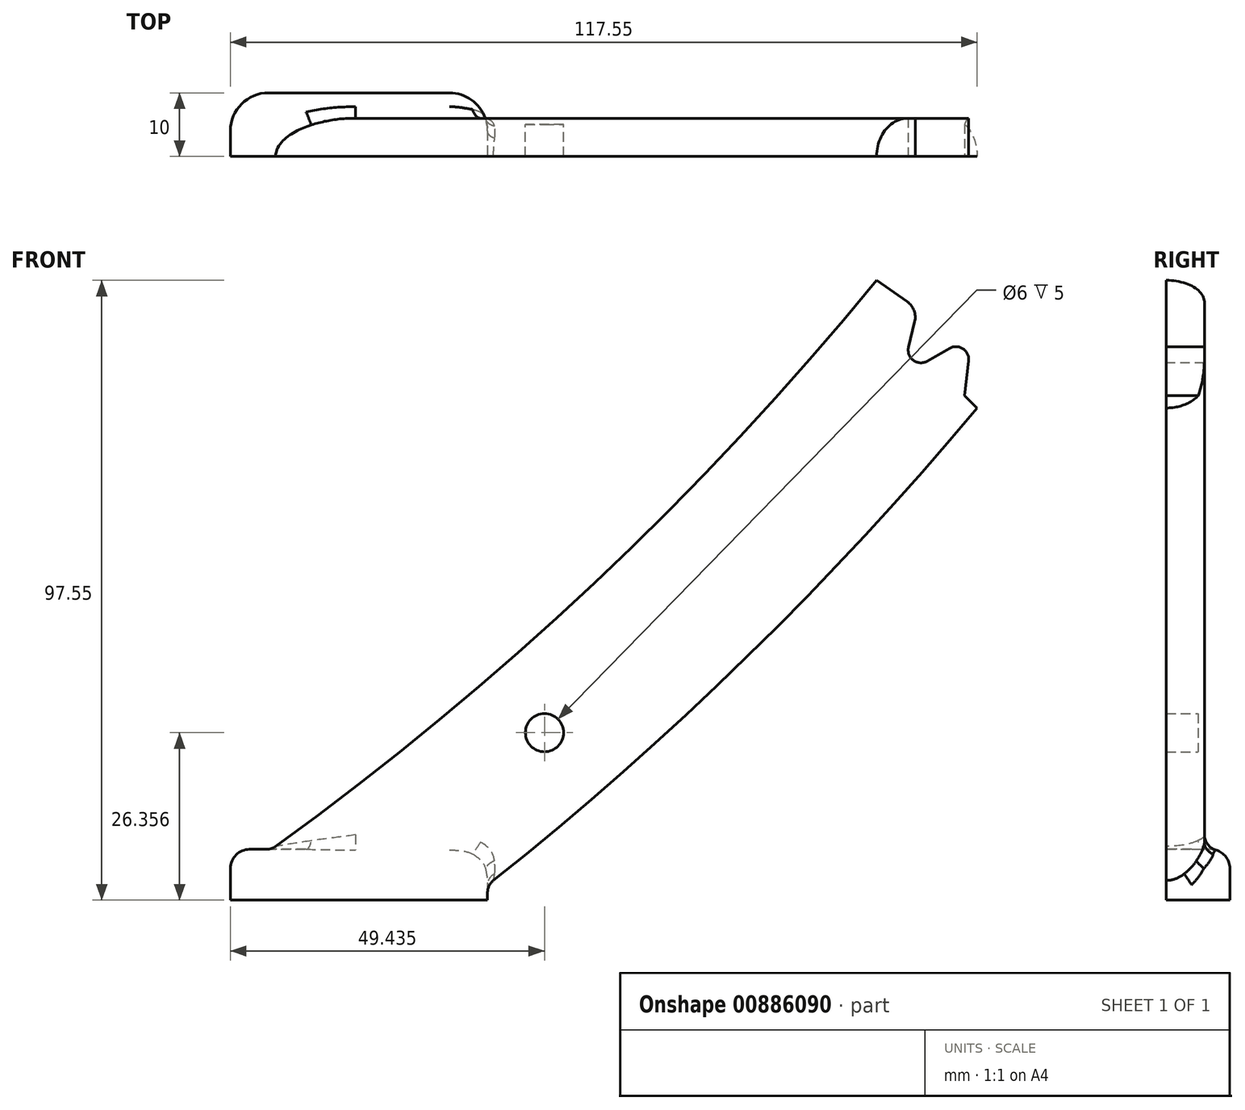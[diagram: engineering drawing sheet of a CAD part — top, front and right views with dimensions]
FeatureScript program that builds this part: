
annotation { "Feature Type Name" : "Feature", "Feature Type Description" : "" }
export const myFeature = defineFeature(function(context is Context, id is Id, definition is map)
    precondition{}
    {
        {
            var Q0;
            Q0=qCreatedBy(makeId("Front.planeOp"),FACE);
            var sketch = newSketch(context, id + "F0", { "sketchPlane" : qUnion([Q0])});
            skLineSegment(sketch, "E0", {"start": v(0, 0) * mm, "end": v(-44.34, 296.7) * mm, "construction": true});
            skLineSegment(sketch, "E1", {"start": v(0, 0) * mm, "end": v(-300, 0) * mm, "construction": true});
            skCircle(sketch, "E2", {"center": v(0, 0) * mm, "radius": 200 * mm, "construction": true});
            skArc(sketch, "E3", {"start": v(-200, 0) * mm, "mid": v(-101.64, 87.58) * mm, "end": v(-29.56, 197.8) * mm});
            skArc(sketch, "E4", {"start": v(-157.53, 0) * mm, "mid": v(-82.7, 71.26) * mm, "end": v(-23.28, 155.8) * mm});
            skLineSegment(sketch, "E5", {"start": v(-23.28, 155.8) * mm, "end": v(-29.56, 197.8) * mm});
            skLineSegment(sketch, "E6", {"start": v(-157.53, 0) * mm, "end": v(-200, 0) * mm});
            skSolve(sketch);
        }
        {
            var Q0;
            Q0 = qSketchRegion(id + "F0", true);
            extrude(context, id + "F1", {"entities" : qUnion([Q0]), "depth" : 12 * mm, "offsetDistance" : 25 * mm});
        }
        {
            var Q0;
            Q0=makeQuery(id+"F1.opExtrude","CAP_EDGE",EDGE,{"disambiguationData":[OSD([sQuery(id+"F0.wireOp",EDGE,"E3")])],"isStart":false});
            var Q1;
            Q1=makeQuery(id+"F1.opExtrude","CAP_EDGE",EDGE,{"disambiguationData":[OSD([sQuery(id+"F0.wireOp",EDGE,"E3")])],"isStart":true});
            var Q2;
            Q2=makeQuery(id+"F1.opExtrude","CAP_EDGE",EDGE,{"disambiguationData":[OSD([sQuery(id+"F0.wireOp",EDGE,"E4")])],"isStart":true});
            var Q3;
            Q3=makeQuery(id+"F1.opExtrude","CAP_EDGE",EDGE,{"disambiguationData":[OSD([sQuery(id+"F0.wireOp",EDGE,"E4")])],"isStart":false});
            fillet(context, id + "F2", {"entities" : qUnion([Q0, Q1, Q2, Q3]), "radius" : 6 * mm, "tangentPropagation" : true, "allowEdgeOverflow" : false});
        }
        {
            var Q0;
            Q0=makeQuery(id+"F1.opExtrude","SWEPT_FACE",FACE,{"disambiguationData":[OSD([sQuery(id+"F0.wireOp",EDGE,"E5")])]});
            var sketch = newSketch(context, id + "F3", { "sketchPlane" : qUnion([Q0])});
            skLineSegment(sketch, "E7.bottom", {"start": v(23, 157.53) * mm, "end": v(-35, 157.53) * mm, "construction": true});
            skLineSegment(sketch, "E7.top", {"start": v(23, 200) * mm, "end": v(-35, 200) * mm, "construction": true});
            skLineSegment(sketch, "E7.left", {"start": v(23, 157.53) * mm, "end": v(23, 200) * mm, "construction": true});
            skLineSegment(sketch, "E7.right", {"start": v(-35, 157.53) * mm, "end": v(-35, 200) * mm, "construction": true});
            skPoint(sketch, "E7.middle", {"position": v(-6, 178.76) * mm});
            skLineSegment(sketch, "E8", {"start": v(-12.34, 197.4) * mm, "end": v(-32.11, 188.18) * mm});
            skLineSegment(sketch, "E9", {"start": v(-32.11, 169.31) * mm, "end": v(-6.84, 157.53) * mm});
            skLineSegment(sketch, "E10", {"start": v(-5.16, 157.53) * mm, "end": v(20.11, 169.31) * mm});
            skLineSegment(sketch, "E11", {"start": v(-35, 183.65) * mm, "end": v(-35, 173.84) * mm});
            skLineSegment(sketch, "E12", {"start": v(23, 173.84) * mm, "end": v(23, 183.65) * mm});
            skPoint(sketch, "E13.visualSharp", {"position": v(23, 185.54) * mm});
            skArc(sketch, "E13.filletArc", {"start": v(23, 183.65) * mm, "mid": v(22.22, 186.34) * mm, "end": v(20.11, 188.18) * mm});
            skPoint(sketch, "E14.visualSharp", {"position": v(23, 170.66) * mm});
            skArc(sketch, "E14.filletArc", {"start": v(20.11, 169.31) * mm, "mid": v(22.22, 171.16) * mm, "end": v(23, 173.84) * mm});
            skPoint(sketch, "E15.visualSharp", {"position": v(-35, 170.66) * mm});
            skArc(sketch, "E15.filletArc", {"start": v(-35, 173.84) * mm, "mid": v(-34.22, 171.16) * mm, "end": v(-32.11, 169.31) * mm});
            skPoint(sketch, "E16.visualSharp", {"position": v(-35, 186.84) * mm});
            skArc(sketch, "E16.filletArc", {"start": v(-32.11, 188.18) * mm, "mid": v(-34.22, 186.34) * mm, "end": v(-35, 183.65) * mm});
            skLineSegment(sketch, "E17", {"start": v(-6.84, 157.53) * mm, "end": v(-5.16, 157.53) * mm});
            skArc(sketch, "E18", {"start": v(0.34, 197.4) * mm, "mid": v(-6, 198.8) * mm, "end": v(-12.34, 197.4) * mm});
            skLineSegment(sketch, "E19.trimOffspring", {"start": v(0.34, 197.4) * mm, "end": v(20.11, 188.18) * mm});
            skSolve(sketch);
        }
        {
            var Q0;
            Q0 = qSketchRegion(id + "F3", true);
            extrude(context, id + "F4", {"entities" : qUnion([Q0]), "operationType" : NewBodyOperationType.ADD, "oppositeDirection" : true, "depth" : 8 * mm, "offsetDistance" : 25 * mm});
        }
        {
            var Q0;
            Q0=makeQuery(id+"F4.boolean.opBoolean","INTERSECT",EDGE,{"derivedFrom":[makeQuery(id+"F2.opFillet","BLEND_FACE",FACE,{"disambiguationData":[OSD([sQuery(id+"F0.wireOp",EDGE,"E3")])]}),makeQuery(id+"F4.opExtrude","CAP_FACE",FACE,{"disambiguationData":[OSD([sQuery(id+"F3.wireOp",EDGE,"RdZrtCav-a8Ya-EYjV-l5Lc-FXPEVfNipvTb"),sQuery(id+"F3.wireOp",EDGE,"E8"),sQuery(id+"F3.wireOp",EDGE,"E9"),sQuery(id+"F3.wireOp",EDGE,"E10"),sQuery(id+"F3.wireOp",EDGE,"E11"),sQuery(id+"F3.wireOp",EDGE,"E12"),sQuery(id+"F3.wireOp",EDGE,"E13.filletArc"),sQuery(id+"F3.wireOp",EDGE,"E14.filletArc"),sQuery(id+"F3.wireOp",EDGE,"E15.filletArc"),sQuery(id+"F3.wireOp",EDGE,"E16.filletArc"),sQuery(id+"F3.wireOp",EDGE,"WmkRQfoL-1Tcq-6rLF-DuZA-oRjccm2ZQQoJ"),sQuery(id+"F3.wireOp",EDGE,"E17")])],"isStart":false})]});
            fillet(context, id + "F5", {"entities" : qUnion([Q0]), "radius" : 5 * mm, "tangentPropagation" : true, "allowEdgeOverflow" : false});
        }
        {
            var Q0;
            Q0=makeQuery(id+"F4.opExtrude","CAP_EDGE",EDGE,{"disambiguationData":[OSD([sQuery(id+"F3.wireOp",EDGE,"E19.trimOffspring")])],"isStart":false});
            fillet(context, id + "F6", {"entities" : qUnion([Q0]), "radius" : 5 * mm, "tangentPropagation" : true, "allowEdgeOverflow" : false});
        }
        {
            var Q0;
            Q0=makeQuery(id+"F1.opExtrude","SWEPT_FACE",FACE,{"disambiguationData":[OSD([sQuery(id+"F0.wireOp",EDGE,"E6")])]});
            var sketch = newSketch(context, id + "F7", { "sketchPlane" : qUnion([Q0])});
            skLineSegment(sketch, "E20.bottom", {"start": v(-160.53, -4) * mm, "end": v(-189, -4) * mm});
            skLineSegment(sketch, "E20.top", {"start": v(-160.53, 16) * mm, "end": v(-189, 16) * mm});
            skLineSegment(sketch, "E20.left", {"start": v(-154.53, 2) * mm, "end": v(-154.53, 10) * mm});
            skLineSegment(sketch, "E20.right", {"start": v(-195, 2) * mm, "end": v(-195, 10) * mm});
            skPoint(sketch, "E20.middle", {"position": v(-174.76, 6) * mm});
            skPoint(sketch, "E21.visualSharp", {"position": v(-195, 16) * mm});
            skArc(sketch, "E21.filletArc", {"start": v(-189, 16) * mm, "mid": v(-193.24, 14.24) * mm, "end": v(-195, 10) * mm});
            skPoint(sketch, "E22.visualSharp", {"position": v(-154.53, 16) * mm});
            skArc(sketch, "E22.filletArc", {"start": v(-154.53, 10) * mm, "mid": v(-156.28, 14.24) * mm, "end": v(-160.53, 16) * mm});
            skPoint(sketch, "E23.visualSharp", {"position": v(-154.53, -4) * mm});
            skArc(sketch, "E23.filletArc", {"start": v(-160.53, -4) * mm, "mid": v(-156.28, -2.24) * mm, "end": v(-154.53, 2) * mm});
            skPoint(sketch, "E24.visualSharp", {"position": v(-195, -4) * mm});
            skArc(sketch, "E24.filletArc", {"start": v(-195, 2) * mm, "mid": v(-193.24, -2.24) * mm, "end": v(-189, -4) * mm});
            skSolve(sketch);
        }
        {
            var Q0;
            Q0 = qSketchRegion(id + "F7", true);
            extrude(context, id + "F8", {"entities" : qUnion([Q0]), "operationType" : NewBodyOperationType.ADD, "oppositeDirection" : true, "depth" : 8 * mm, "offsetDistance" : 25 * mm});
        }
        {
            var Q0;
            Q0=makeQuery(id+"F8.opExtrude","CAP_EDGE",EDGE,{"disambiguationData":[OSD([sQuery(id+"F7.wireOp",EDGE,"E20.bottom")])],"isStart":false});
            fillet(context, id + "F9", {"entities" : qUnion([Q0]), "radius" : 3 * mm, "tangentPropagation" : true, "allowEdgeOverflow" : false});
        }
        {
            var Q0;
            Q0=makeQuery(id+"F8.boolean.opBoolean","INTERSECT",EDGE,{"derivedFrom":[makeQuery(id+"F1.opExtrude","CAP_FACE",FACE,{"disambiguationData":[OSD([sQuery(id+"F0.wireOp",EDGE,"E3"),sQuery(id+"F0.wireOp",EDGE,"E4"),sQuery(id+"F0.wireOp",EDGE,"E5"),sQuery(id+"F0.wireOp",EDGE,"E6")])],"isStart":true}),makeQuery(id+"F8.opExtrude","CAP_FACE",FACE,{"disambiguationData":[OSD([sQuery(id+"F7.wireOp",EDGE,"E20.bottom"),sQuery(id+"F7.wireOp",EDGE,"E20.top"),sQuery(id+"F7.wireOp",EDGE,"E20.left"),sQuery(id+"F7.wireOp",EDGE,"E20.right"),sQuery(id+"F7.wireOp",EDGE,"E21.filletArc"),sQuery(id+"F7.wireOp",EDGE,"E22.filletArc"),sQuery(id+"F7.wireOp",EDGE,"E23.filletArc"),sQuery(id+"F7.wireOp",EDGE,"E24.filletArc")])],"isStart":false})]});
            fillet(context, id + "F10", {"entities" : qUnion([Q0]), "radius" : 2.5 * mm, "tangentPropagation" : true, "allowEdgeOverflow" : false});
        }
        {
            var Q0;
            Q0=makeQuery(id+"F8.boolean.opBoolean","MERGE",FACE,{"derivedFrom":[makeQuery(id+"F1.opExtrude","SWEPT_FACE",FACE,{"disambiguationData":[OSD([sQuery(id+"F0.wireOp",EDGE,"E6")])]}),makeQuery(id+"F8.opExtrude","CAP_FACE",FACE,{"disambiguationData":[OSD([sQuery(id+"F7.wireOp",EDGE,"E20.bottom"),sQuery(id+"F7.wireOp",EDGE,"E20.top"),sQuery(id+"F7.wireOp",EDGE,"E20.left"),sQuery(id+"F7.wireOp",EDGE,"E20.right"),sQuery(id+"F7.wireOp",EDGE,"E21.filletArc"),sQuery(id+"F7.wireOp",EDGE,"E22.filletArc"),sQuery(id+"F7.wireOp",EDGE,"E23.filletArc"),sQuery(id+"F7.wireOp",EDGE,"E24.filletArc")])],"isStart":true})]});
            var sketch = newSketch(context, id + "F11", { "sketchPlane" : qUnion([Q0])});
            skArc(sketch, "E25", {"start": v(-194.9, 0.87) * mm, "mid": v(-192.82, -2.62) * mm, "end": v(-189, -4) * mm});
            skArc(sketch, "E26", {"start": v(-189, 16) * mm, "mid": v(-192.82, 14.62) * mm, "end": v(-194.9, 11.13) * mm});
            skLineSegment(sketch, "E27", {"start": v(-189, -4) * mm, "end": v(-189.9, -7.83) * mm});
            skLineSegment(sketch, "E28", {"start": v(-189.9, -7.83) * mm, "end": v(-199.49, -1.04) * mm});
            skLineSegment(sketch, "E29", {"start": v(-199.49, -1.04) * mm, "end": v(-201.87, 5.8) * mm});
            skLineSegment(sketch, "E30", {"start": v(-201.87, 5.8) * mm, "end": v(-200.5, 12.71) * mm});
            skLineSegment(sketch, "E31", {"start": v(-200.5, 12.71) * mm, "end": v(-193.47, 21.42) * mm});
            skLineSegment(sketch, "E32", {"start": v(-193.47, 21.42) * mm, "end": v(-189, 16) * mm});
            skLineSegment(sketch, "E33.0.1", {"start": v(-195, 10) * mm, "end": v(-195, 2) * mm});
            skFitSpline(sketch, "E33.0.3", {"points": [v(-195, 2) * mm, v(-195, 4.67) * mm, v(-195, 7.33) * mm, v(-195, 10) * mm]});
            skArc(sketch, "E34", {"start": v(-195, 2) * mm, "mid": v(-194.97, 1.43) * mm, "end": v(-194.9, 0.87) * mm});
            skArc(sketch, "E35", {"start": v(-194.9, 11.13) * mm, "mid": v(-194.97, 10.57) * mm, "end": v(-195, 10) * mm});
            skSolve(sketch);
        }
        {
            var Q0;
            Q0 = qSketchRegion(id + "F11", true);
            extrude(context, id + "F12", {"entities" : qUnion([Q0]), "operationType" : NewBodyOperationType.REMOVE, "oppositeDirection" : true, "depth" : 25 * mm, "offsetDistance" : 25 * mm});
        }
        {
            var Q0;
            Q0=makeQuery(id+"F4.boolean.opBoolean","MERGE",FACE,{"derivedFrom":[makeQuery(id+"F1.opExtrude","SWEPT_FACE",FACE,{"disambiguationData":[OSD([sQuery(id+"F0.wireOp",EDGE,"E5")])]}),makeQuery(id+"F4.opExtrude","CAP_FACE",FACE,{"disambiguationData":[OSD([sQuery(id+"F3.wireOp",EDGE,"E8"),sQuery(id+"F3.wireOp",EDGE,"E9"),sQuery(id+"F3.wireOp",EDGE,"E10"),sQuery(id+"F3.wireOp",EDGE,"E11"),sQuery(id+"F3.wireOp",EDGE,"E12"),sQuery(id+"F3.wireOp",EDGE,"E13.filletArc"),sQuery(id+"F3.wireOp",EDGE,"E14.filletArc"),sQuery(id+"F3.wireOp",EDGE,"E15.filletArc"),sQuery(id+"F3.wireOp",EDGE,"E16.filletArc"),sQuery(id+"F3.wireOp",EDGE,"E17"),sQuery(id+"F3.wireOp",EDGE,"E18"),sQuery(id+"F3.wireOp",EDGE,"E19.trimOffspring")])],"isStart":true})]});
            var sketch = newSketch(context, id + "F13", { "sketchPlane" : qUnion([Q0])});
            skArc(sketch, "E36.0.1", {"start": v(0.34, 197.4) * mm, "mid": v(-6, 198.8) * mm, "end": v(-12.34, 197.4) * mm});
            skArc(sketch, "E36.0.3", {"start": v(-12.34, 197.4) * mm, "mid": v(-10.74, 198.04) * mm, "end": v(-9.08, 198.5) * mm});
            skArc(sketch, "E36.0.4", {"start": v(-2.92, 198.5) * mm, "mid": v(-6, 198.8) * mm, "end": v(-9.08, 198.5) * mm});
            skArc(sketch, "E36.0.5", {"start": v(-2.92, 198.5) * mm, "mid": v(-1.26, 198.04) * mm, "end": v(0.34, 197.4) * mm});
            skLineSegment(sketch, "E37", {"start": v(-12.34, 197.4) * mm, "end": v(-12.34, 202.28) * mm});
            skLineSegment(sketch, "E38", {"start": v(-12.34, 202.28) * mm, "end": v(-2.7, 206.24) * mm});
            skLineSegment(sketch, "E39", {"start": v(-2.7, 206.24) * mm, "end": v(2.38, 202.78) * mm});
            skLineSegment(sketch, "E40", {"start": v(2.38, 202.78) * mm, "end": v(0.34, 197.4) * mm});
            skSolve(sketch);
        }
        {
            var Q0;
            Q0 = qSketchRegion(id + "F13", true);
            extrude(context, id + "F14", {"entities" : qUnion([Q0]), "operationType" : NewBodyOperationType.REMOVE, "oppositeDirection" : true, "depth" : 25 * mm, "offsetDistance" : 25 * mm});
        }
        {
            var Q0;
            Q0=qCreatedBy(makeId("Front.planeOp"),FACE);
            var sketch = newSketch(context, id + "F15", { "sketchPlane" : qUnion([Q0])});
            skLineSegment(sketch, "E41", {"start": v(0, 0) * mm, "end": v(-79.4, 79.4) * mm});
            skLineSegment(sketch, "E42", {"start": v(-212.8, 212.8) * mm, "end": v(-212.8, -12.4) * mm});
            skLineSegment(sketch, "E43", {"start": v(-212.8, -12.4) * mm, "end": v(0, 0) * mm});
            skLineSegment(sketch, "E44", {"start": v(-79.4, 79.4) * mm, "end": v(-78.78, 84.89) * mm});
            skLineSegment(sketch, "E45", {"start": v(-81.76, 86.85) * mm, "end": v(-85.31, 84.83) * mm});
            skLineSegment(sketch, "E46", {"start": v(-88.25, 87.04) * mm, "end": v(-87.28, 91.02) * mm});
            skLineSegment(sketch, "E47", {"start": v(-88.47, 94.2) * mm, "end": v(-108.49, 108.19) * mm});
            skLineSegment(sketch, "E48", {"start": v(-104.8, 104.8) * mm, "end": v(-108.49, 108.19) * mm});
            skLineSegment(sketch, "E49.trimOffspring", {"start": v(-104.8, 104.8) * mm, "end": v(-212.8, 212.8) * mm});
            skPoint(sketch, "E50.visualSharp", {"position": v(-86.8, 93.02) * mm});
            skArc(sketch, "E50.filletArc", {"start": v(-87.28, 91.02) * mm, "mid": v(-87.39, 92.8) * mm, "end": v(-88.47, 94.2) * mm});
            skPoint(sketch, "E51.visualSharp", {"position": v(-89.34, 82.54) * mm});
            skArc(sketch, "E51.filletArc", {"start": v(-88.25, 87.04) * mm, "mid": v(-87.5, 84.97) * mm, "end": v(-85.31, 84.83) * mm});
            skPoint(sketch, "E52.visualSharp", {"position": v(-78.35, 88.79) * mm});
            skArc(sketch, "E52.filletArc", {"start": v(-78.78, 84.89) * mm, "mid": v(-79.67, 86.78) * mm, "end": v(-81.76, 86.85) * mm});
            skSolve(sketch);
        }
        {
            var Q0;
            Q0=makeQuery(id+"F1.opExtrude","CAP_FACE",FACE,{"disambiguationData":[OSD([sQuery(id+"F0.wireOp",EDGE,"E3"),sQuery(id+"F0.wireOp",EDGE,"E4"),sQuery(id+"F0.wireOp",EDGE,"E5"),sQuery(id+"F0.wireOp",EDGE,"E6")])],"isStart":true});
            cPlane(context, id + "F16", {"entities" : qUnion([Q0]), "cplaneType" : CPlaneType.OFFSET, "offset" : 6 * mm, "oppositeDirection" : true, "width" : 150 * mm, "height" : 150 * mm});
        }
        {
            var Q0;
            Q0=qCreatedBy(id+"F16.planeOp",FACE);
            var sketch = newSketch(context, id + "F17", { "sketchPlane" : qUnion([Q0])});
            skCircle(sketch, "E53", {"center": v(45.28, 144.4) * mm, "radius": 3 * mm});
            skCircle(sketch, "E54", {"center": v(145.56, 26.36) * mm, "radius": 3 * mm});
            skSolve(sketch);
        }
        {
            var Q0;
            Q0 = qSketchRegion(id + "F17", true);
            extrude(context, id + "F18", {"entities" : qUnion([Q0]), "operationType" : NewBodyOperationType.REMOVE, "oppositeDirection" : true, "depth" : 5 * mm, "offsetDistance" : 25 * mm, "hasSecondDirection" : true, "secondDirectionOppositeDirection" : false, "secondDirectionDepth" : 5 * mm});
        }
        {
            var Q0;
            Q0=qCreatedBy(id+"F16.planeOp",FACE);
            var sketch = newSketch(context, id + "F19", { "sketchPlane" : qUnion([Q0])});
            skLineSegment(sketch, "E55.bottom", {"start": v(247.9, -39.19) * mm, "end": v(-74.6, -39.19) * mm});
            skLineSegment(sketch, "E55.top", {"start": v(247.9, 213.74) * mm, "end": v(-74.6, 213.74) * mm});
            skLineSegment(sketch, "E55.left", {"start": v(247.9, -39.19) * mm, "end": v(247.9, 213.74) * mm});
            skLineSegment(sketch, "E55.right", {"start": v(-74.6, -39.19) * mm, "end": v(-74.6, 213.74) * mm});
            skPoint(sketch, "E55.middle", {"position": v(86.65, 87.27) * mm});
            skSolve(sketch);
        }
        {
            var Q0;
            Q0 = qSketchRegion(id + "F15", true);
            extrude(context, id + "F20", {"entities" : qUnion([Q0]), "operationType" : NewBodyOperationType.INTERSECT, "oppositeDirection" : true, "depth" : 50 * mm, "offsetDistance" : 25 * mm, "hasSecondDirection" : true, "secondDirectionOppositeDirection" : false, "secondDirectionDepth" : 50 * mm});
        }
        {
            var Q0;
            Q0 = qSketchRegion(id + "F19", true);
            extrude(context, id + "F21", {"entities" : qUnion([Q0]), "operationType" : NewBodyOperationType.INTERSECT, "depth" : 50 * mm, "offsetDistance" : 25 * mm});
        }
    });
